# Revit family: Gira_277626
name_source: partatom
category: Electrical Fixtures
revit_build: Autodesk Revit 2017 (Build: 20160225_1515(x64)
units: mm (PartAtom-declared; Revit-internal decimal feet)

## family parameters
Cut with Voids When Loaded = No
Host = Face
Maintain Annotation Orientation = Yes
Part Type = Normal
Room Calculation Point = No
Round Connector Dimension = Use Diameter
Shared = No

## types (1)
- Steckd. BS 13 A SH System 55 F Alu
    Abschließbar = No
    Anschlussart = Schraubklemme
    Antibakterielle Behandlung = No
    Anzahl der Einheiten = 1
    Anzahl der Module (bei Modulbauweise) = 1
    Anzahl der Steckdosen schaltbar = 0
    Aufdruck/Kennzeichnung = ohne Aufdruck
    Ausführung = British Standard
    Auswurfmechanismus = No
    Available = Yes
    Befestigungsart = Befestigung mit Schraube
    Category = Steckdose
    Cremeweiß glänzend = Cremeweiß glänzend
    Data sheet (1) = https://katalog.gira.de
    Default Elevation = 1219 mm
    Farbe = aluminium
    Fehlerstromschutz = No
    Für "erschwerte Bedingungen" (nach VDE) = No
    GTIN = 4010337079361
    Geeignet für Schutzart (IP) = IP20
    HAN = 277626
    Halogenfrei = No
    HeinzeBIM = https://bimportal.heinze.de
    Isolierter Einbau = No
    Manufacturer URL = https://www.gira.de
    Mit Durchschleiffunktion = No
    Mit Ein-/Ausschalter = No
    Mit Feinsicherung = No
    Mit Funktionsbeleuchtung = No
    Mit Klappdeckel = No
    Mit Orientierungsbeleuchtung = No
    Mit Signallampe = No
    Mit eingebauter USB-Spannungsversorgung = No
    Mit erhöhtem Berührungsschutz = Yes
    Model = SYS55_Steckdose
    Montageart = unter Putz
    Name = Steckd. BS 13 A SH System 55 F Alu
    Nennspannung = 250 Volt
    Nennstrom = 13 Ampere
    Oberfläche = sonstige
    Region = DE
    Schutzkontakt = No
    Schutzleiterkontakt rund = No
    Sonderstromversorgung = ohne Sonderstromversorgung
    Textfeld/Beschriftungsfläche = No
    Transparent = No
    URL = http://katalog.gira.de
    Verdrehter Zentraleinsatz = No
    Werkstoff = sonstige
    Werkstoffgüte = sonstige
    Überspannungsschutz = No

## geometry (parser evidence)
native form markers: Blend x2, Sweep x4
no freeform markers — native parametric forms only
